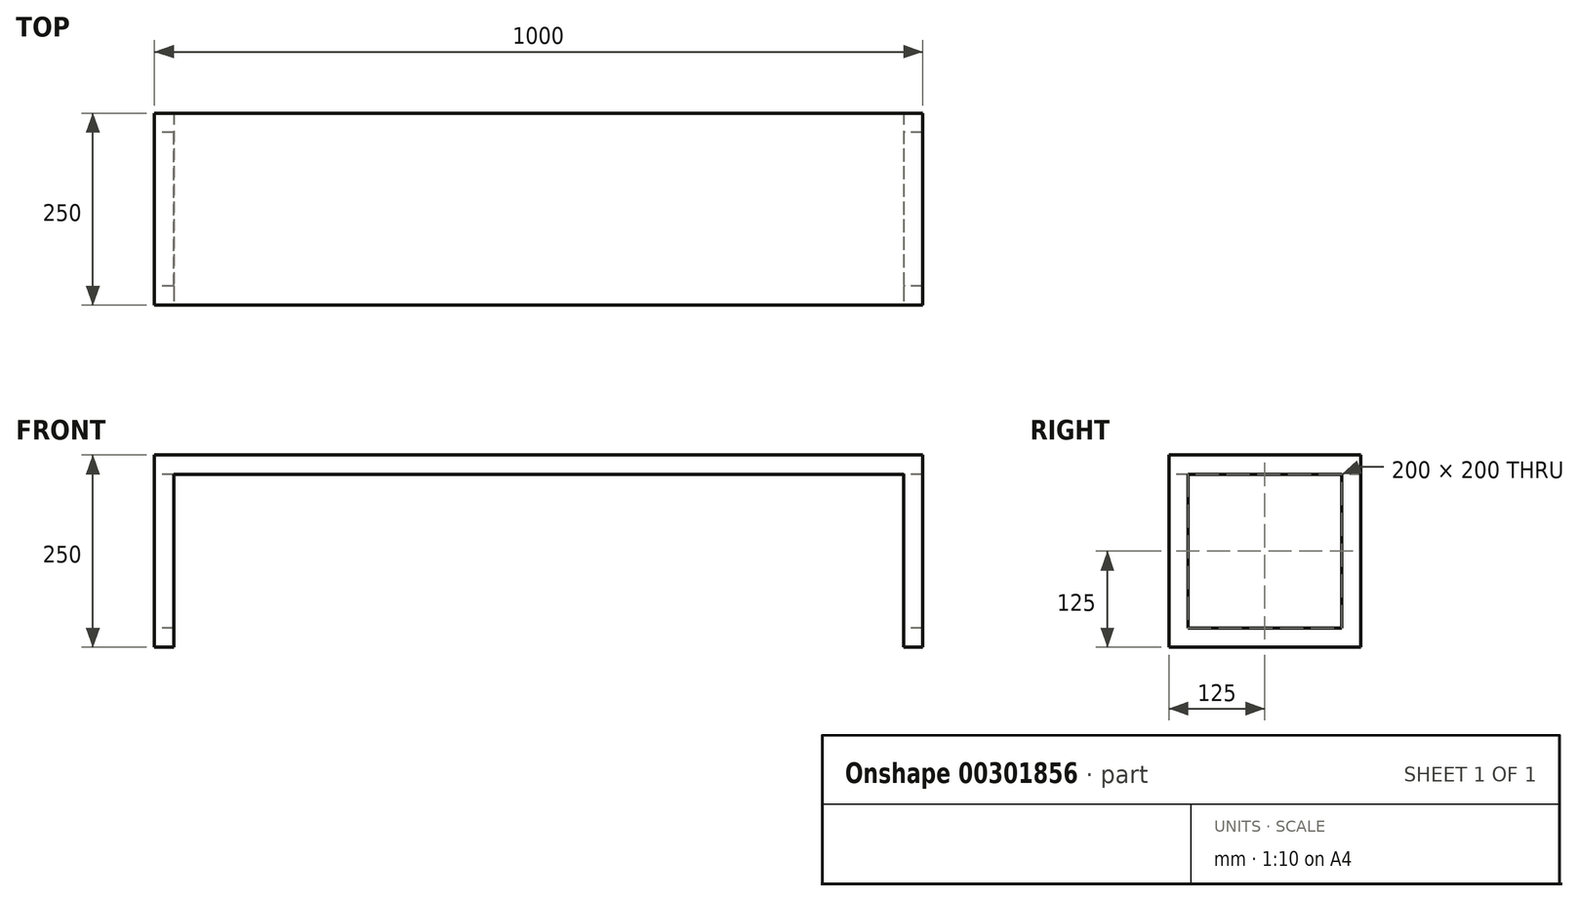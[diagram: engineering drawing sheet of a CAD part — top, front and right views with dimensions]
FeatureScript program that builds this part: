
annotation { "Feature Type Name" : "Feature", "Feature Type Description" : "" }
export const myFeature = defineFeature(function(context is Context, id is Id, definition is map)
    precondition{}
    {
        {
            var Q0;
            Q0=qCreatedBy(makeId("Front.planeOp"),FACE);
            var sketch = newSketch(context, id + "F0", { "sketchPlane" : qUnion([Q0])});
            skLineSegment(sketch, "E0.bottom", {"start": v(0, 0) * mm, "end": v(2000, 0) * mm});
            skLineSegment(sketch, "E0.top", {"start": v(0, 500) * mm, "end": v(2000, 500) * mm});
            skLineSegment(sketch, "E0.left", {"start": v(0, 0) * mm, "end": v(0, 500) * mm});
            skLineSegment(sketch, "E0.right", {"start": v(2000, 0) * mm, "end": v(2000, 500) * mm});
            skSolve(sketch);
        }
        {
            var Q0;
            Q0=makeQuery(id+"F0.imprint","IMPRINT",FACE,{"disambiguationData":[TD([[makeQuery(id+"F0.imprint","IMPRINT",EDGE,{"derivedFrom":sQuery(id+"F0.wireOp",EDGE,"E0.bottom")}),1.0]])]});
            extrude(context, id + "F1", {"entities" : qUnion([Q0]), "depth" : 500 * mm});
        }
        {
            var Q0;
            Q0=makeQuery(id+"F1.opExtrude","CAP_FACE",FACE,{"disambiguationData":[OSD([sQuery(id+"F0.wireOp",EDGE,"E0.bottom"),sQuery(id+"F0.wireOp",EDGE,"E0.top"),sQuery(id+"F0.wireOp",EDGE,"E0.left"),sQuery(id+"F0.wireOp",EDGE,"E0.right")])],"isStart":false});
            var sketch = newSketch(context, id + "F2", { "sketchPlane" : qUnion([Q0])});
            skLineSegment(sketch, "E1", {"start": v(50, 0) * mm, "end": v(50, 450) * mm});
            skLineSegment(sketch, "E2", {"start": v(50, 450) * mm, "end": v(1950, 450) * mm});
            skLineSegment(sketch, "E3", {"start": v(1950, 450) * mm, "end": v(1950, 0) * mm});
            skSolve(sketch);
        }
        {
            var Q0;
            {var subQ0=sQuery(id+"F2.wireOp",EDGE,"E1");Q0=makeQuery(id+"F2.imprint","IMPRINT",FACE,{"disambiguationData":[TD([[makeQuery(id+"F2.imprint","IMPRINT",EDGE,{"derivedFrom":subQ0}),-1.0]])]});}
            extrude(context, id + "F3", {"entities" : qUnion([Q0]), "operationType" : NewBodyOperationType.REMOVE, "endBound" : BoundingType.THROUGH_ALL, "oppositeDirection" : true, "depth" : 25 * mm});
        }
        {
            var Q0;
            Q0=makeQuery(id+"F1.opExtrude","SWEPT_FACE",FACE,{"disambiguationData":[OSD([sQuery(id+"F0.wireOp",EDGE,"E0.left")])]});
            var sketch = newSketch(context, id + "F4", { "sketchPlane" : qUnion([Q0])});
            skLineSegment(sketch, "E4.bottom", {"start": v(50, 450) * mm, "end": v(450, 450) * mm});
            skLineSegment(sketch, "E4.top", {"start": v(50, 50) * mm, "end": v(450, 50) * mm});
            skLineSegment(sketch, "E4.left", {"start": v(50, 450) * mm, "end": v(50, 50) * mm});
            skLineSegment(sketch, "E4.right", {"start": v(450, 450) * mm, "end": v(450, 50) * mm});
            skSolve(sketch);
        }
        {
            var Q0;
            Q0=makeQuery(id+"F4.imprint","IMPRINT",FACE,{"disambiguationData":[TD([[makeQuery(id+"F4.imprint","IMPRINT",EDGE,{"derivedFrom":sQuery(id+"F4.wireOp",EDGE,"E4.bottom")}),-1.0]])]});
            extrude(context, id + "F5", {"entities" : qUnion([Q0]), "operationType" : NewBodyOperationType.REMOVE, "endBound" : BoundingType.THROUGH_ALL, "oppositeDirection" : true, "depth" : 25 * mm});
        }
        {
            var Q0;
            Q0=makeQuery(id+"F1.opExtrude","SWEPT_BODY",BODY,{"disambiguationData":[OSD([sQuery(id+"F0.wireOp",EDGE,"E0.bottom"),sQuery(id+"F0.wireOp",EDGE,"E0.top"),sQuery(id+"F0.wireOp",EDGE,"E0.left"),sQuery(id+"F0.wireOp",EDGE,"E0.right")])]});
            var Q1;
            Q1=qCreatedBy(makeId("Origin.pointOp"),VERTEX);
            transform(context, id + "F6", {"entities" : qUnion([Q0]), "transformType" : TransformType.SCALE_UNIFORMLY, "scale" : 0.5, "scalePoint" : qUnion([Q1]), "makeCopy" : false});
        }
    });
